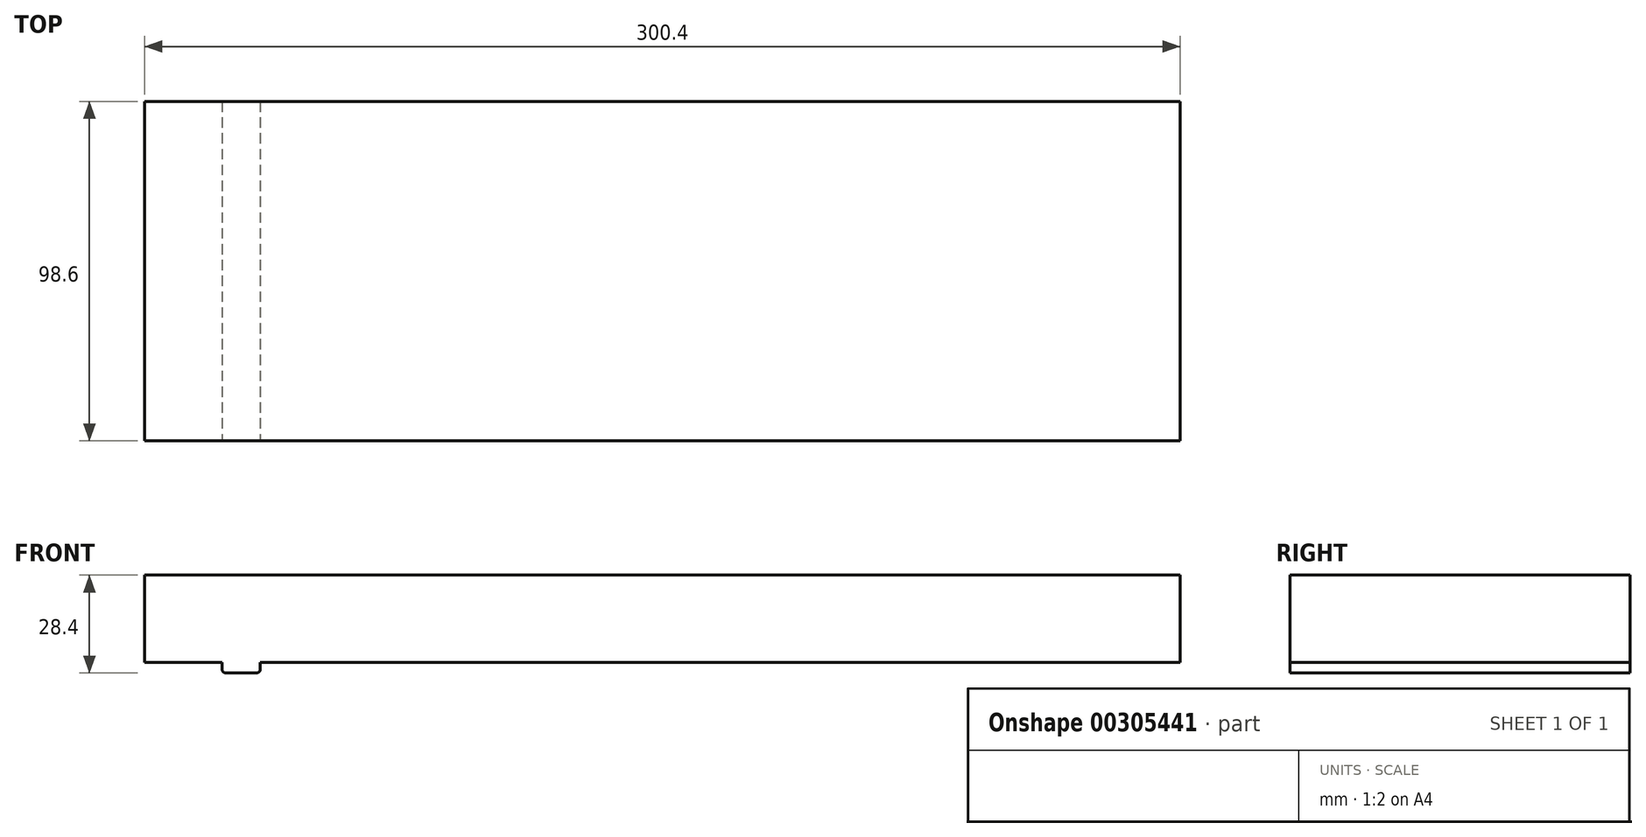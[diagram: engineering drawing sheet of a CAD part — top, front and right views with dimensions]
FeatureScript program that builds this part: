
annotation { "Feature Type Name" : "Feature", "Feature Type Description" : "" }
export const myFeature = defineFeature(function(context is Context, id is Id, definition is map)
    precondition{}
    {
        {
            var Q0;
            Q0=qCreatedBy(makeId("Front.planeOp"),FACE);
            var sketch = newSketch(context, id + "F0", { "sketchPlane" : qUnion([Q0])});
            skLineSegment(sketch, "E0", {"start": v(0, 0) * mm, "end": v(22.5, 0) * mm});
            skLineSegment(sketch, "E1", {"start": v(300.4, 0) * mm, "end": v(300.4, 25.4) * mm});
            skLineSegment(sketch, "E2", {"start": v(300.4, 25.4) * mm, "end": v(0, 25.4) * mm});
            skLineSegment(sketch, "E3", {"start": v(0, 25.4) * mm, "end": v(0, 0) * mm});
            skPoint(sketch, "E4.visualSharp", {"position": v(22.5, -3) * mm});
            skPoint(sketch, "E5.visualSharp", {"position": v(33.5, -3) * mm});
            skLineSegment(sketch, "E6.trimOffspring", {"start": v(33.5, 0) * mm, "end": v(300.4, 0) * mm});
            skLineSegment(sketch, "E7", {"start": v(22.5, -2) * mm, "end": v(22.5, 0) * mm});
            skLineSegment(sketch, "E8", {"start": v(33.5, -2) * mm, "end": v(33.5, 0) * mm});
            skLineSegment(sketch, "E9", {"start": v(32.5, -3) * mm, "end": v(23.5, -3) * mm});
            skArc(sketch, "E10.filletArc", {"start": v(22.5, -2) * mm, "mid": v(22.8, -2.7) * mm, "end": v(23.5, -3) * mm});
            skArc(sketch, "E11.filletArc", {"start": v(32.5, -3) * mm, "mid": v(33.2, -2.7) * mm, "end": v(33.5, -2) * mm});
            skSolve(sketch);
        }
        {
            var Q0;
            Q0=makeQuery(id+"F0.imprint","IMPRINT",FACE,{"disambiguationData":[TD([[makeQuery(id+"F0.imprint","IMPRINT",EDGE,{"derivedFrom":sQuery(id+"F0.wireOp",EDGE,"E0")}),1.0]])]});
            extrude(context, id + "F1", {"entities" : qUnion([Q0]), "oppositeDirection" : true, "depth" : 98.6 * mm});
        }
    });
